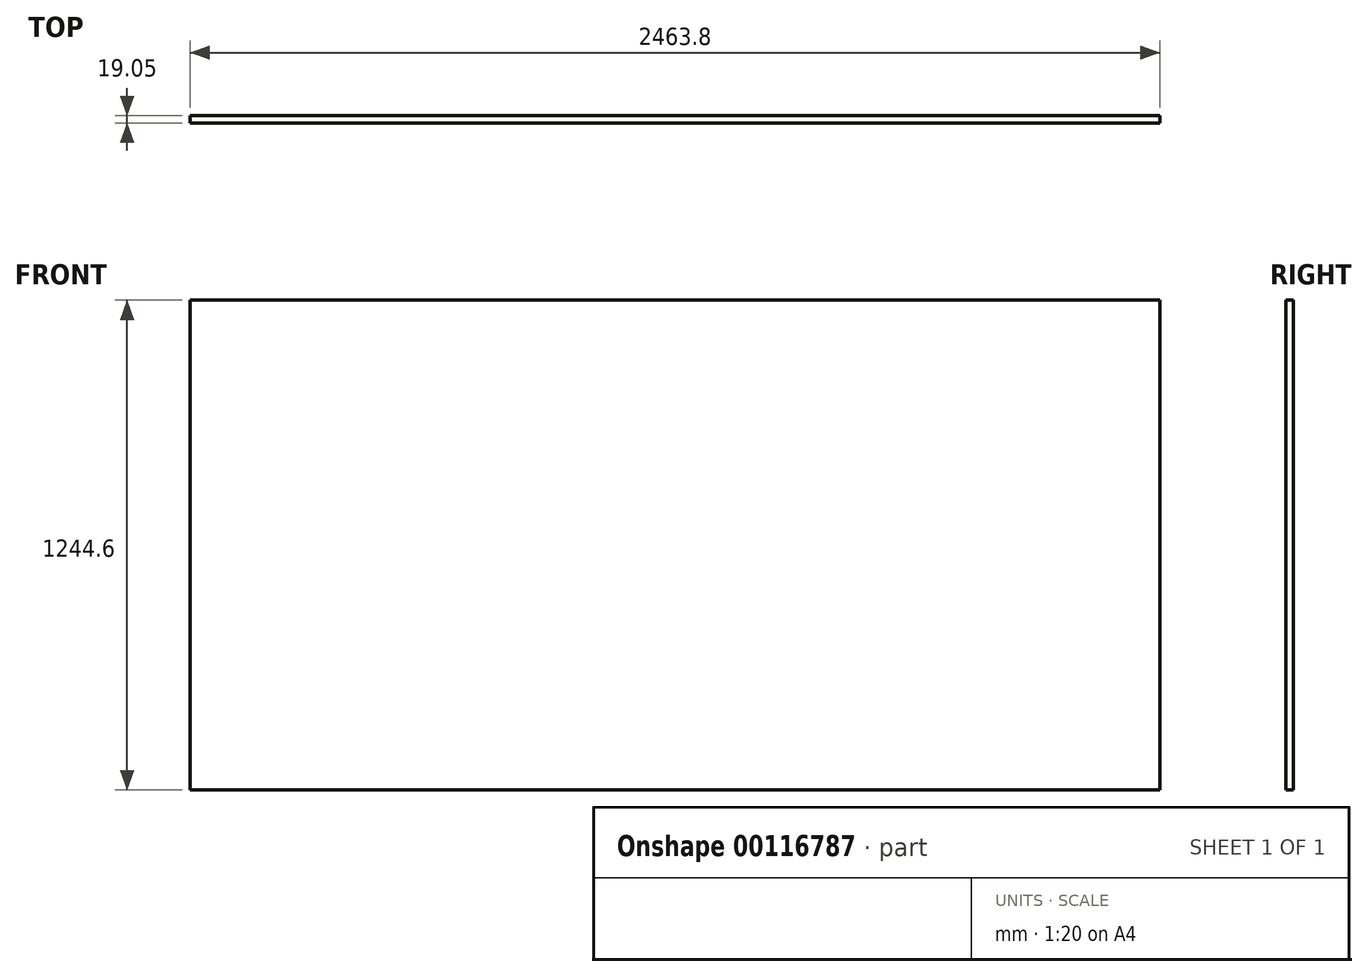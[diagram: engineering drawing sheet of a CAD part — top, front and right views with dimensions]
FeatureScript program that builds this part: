
annotation { "Feature Type Name" : "Feature", "Feature Type Description" : "" }
export const myFeature = defineFeature(function(context is Context, id is Id, definition is map)
    precondition{}
    {
        {
            var Q0;
            Q0=qCreatedBy(makeId("Front.planeOp"),FACE);
            var sketch = newSketch(context, id + "F0", { "sketchPlane" : qUnion([Q0])});
            skLineSegment(sketch, "E0.bottom", {"start": v(0, 0) * mm, "end": v(2463.8, 0) * mm});
            skLineSegment(sketch, "E0.top", {"start": v(0, 1244.6) * mm, "end": v(2463.8, 1244.6) * mm});
            skLineSegment(sketch, "E0.left", {"start": v(0, 0) * mm, "end": v(0, 1244.6) * mm});
            skLineSegment(sketch, "E0.right", {"start": v(2463.8, 0) * mm, "end": v(2463.8, 1244.6) * mm});
            skSolve(sketch);
        }
        {
            var Q0;
            Q0 = qSketchRegion(id + "F0", true);
            extrude(context, id + "F1", {"entities" : qUnion([Q0]), "depth" : 19.05 * mm});
        }
    });
